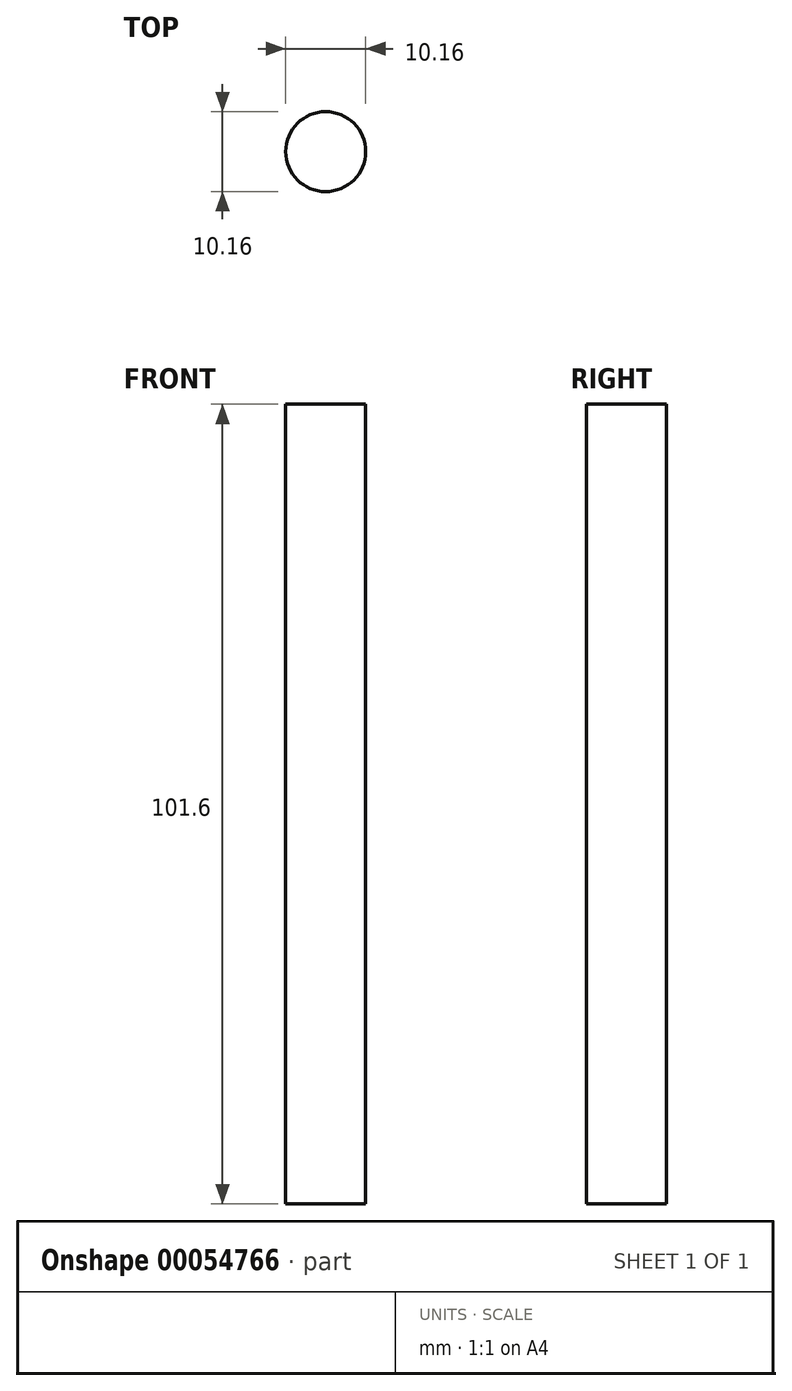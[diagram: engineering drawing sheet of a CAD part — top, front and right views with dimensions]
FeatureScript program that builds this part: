
annotation { "Feature Type Name" : "Feature", "Feature Type Description" : "" }
export const myFeature = defineFeature(function(context is Context, id is Id, definition is map)
    precondition{}
    {
        {
            var Q0;
            Q0=qCreatedBy(makeId("Top.planeOp"),FACE);
            var sketch = newSketch(context, id + "F0", { "sketchPlane" : qUnion([Q0])});
            skCircle(sketch, "E0", {"center": v(0, 0) * mm, "radius": 5.08 * mm});
            skSolve(sketch);
        }
        {
            var Q0;
            Q0=makeQuery(id+"F0.imprint","IMPRINT",FACE,{"disambiguationData":[TD([[makeQuery(id+"F0.imprint","IMPRINT",EDGE,{"derivedFrom":sQuery(id+"F0.wireOp",EDGE,"E0")}),1.0]])]});
            extrude(context, id + "F1", {"entities" : qUnion([Q0]), "depth" : 101.6 * mm});
        }
    });
